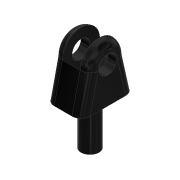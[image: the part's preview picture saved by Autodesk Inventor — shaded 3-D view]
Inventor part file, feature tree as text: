
AUTODESK INVENTOR PART (.ipt)
format: ipt  version: 2020.2 (Build 242310000, 310)  size: 191,488 bytes
history: native  units: mm
features: extrude x7, sketch x7, fillet x1
ambient origin geometry x8: Origin, YZ Plane, XZ Plane, XY Plane, X Axis, Y Axis, Z Axis, Center Point
bodies: Solid1 (feature_tree)
feature tree (15):
  extrude  "Extrusion1"  Depth=21.0mm
  extrude  "Extrusion2"  Depth=15.0mm
  extrude  "Extrusion3"  Depth=5.0mm TaperAngle=0.0deg
  sketch  "Sketch5"  dims[d7=10.0mm d8=0.0mm d9=5.0mm d10=0.0mm d11=10.0mm]
  extrude  "Extrusion4"  Depth=5.0mm TaperAngle=0.0deg
  fillet  "Fillet1"  Radius=10.0mm
  extrude  "Extrusion5"  Depth=25.0mm TaperAngle=0.0deg
  extrude  "Extrusion6"  Depth=20.0mm TaperAngle=0.0deg
  extrude  "Extrusion7"  Depth=6.0mm
  sketch  "Sketch1"  dims[d0=10.0mm d1=21.0mm]
  sketch  "Sketch2"  dims[d2=20.0mm d3=15.0mm]
  sketch  "Sketch4"  dims[d4=30.0mm d5=5.0mm d6=0.0mm]
  sketch  "Sketch6"  dims[d12=5.0mm d13=25.0mm d14=0.0mm]
  sketch  "Sketch7"  dims[d15=3.25mm d16=20.0mm d17=0.0mm]
  sketch  "Sketch8"  dims[d18=5.0mm d19=3.0mm d20=10.0mm d21=0.0mm d22=3.0mm d23=2.0mm d24=6.0mm d25=10.0mm d26=0.0mm]
